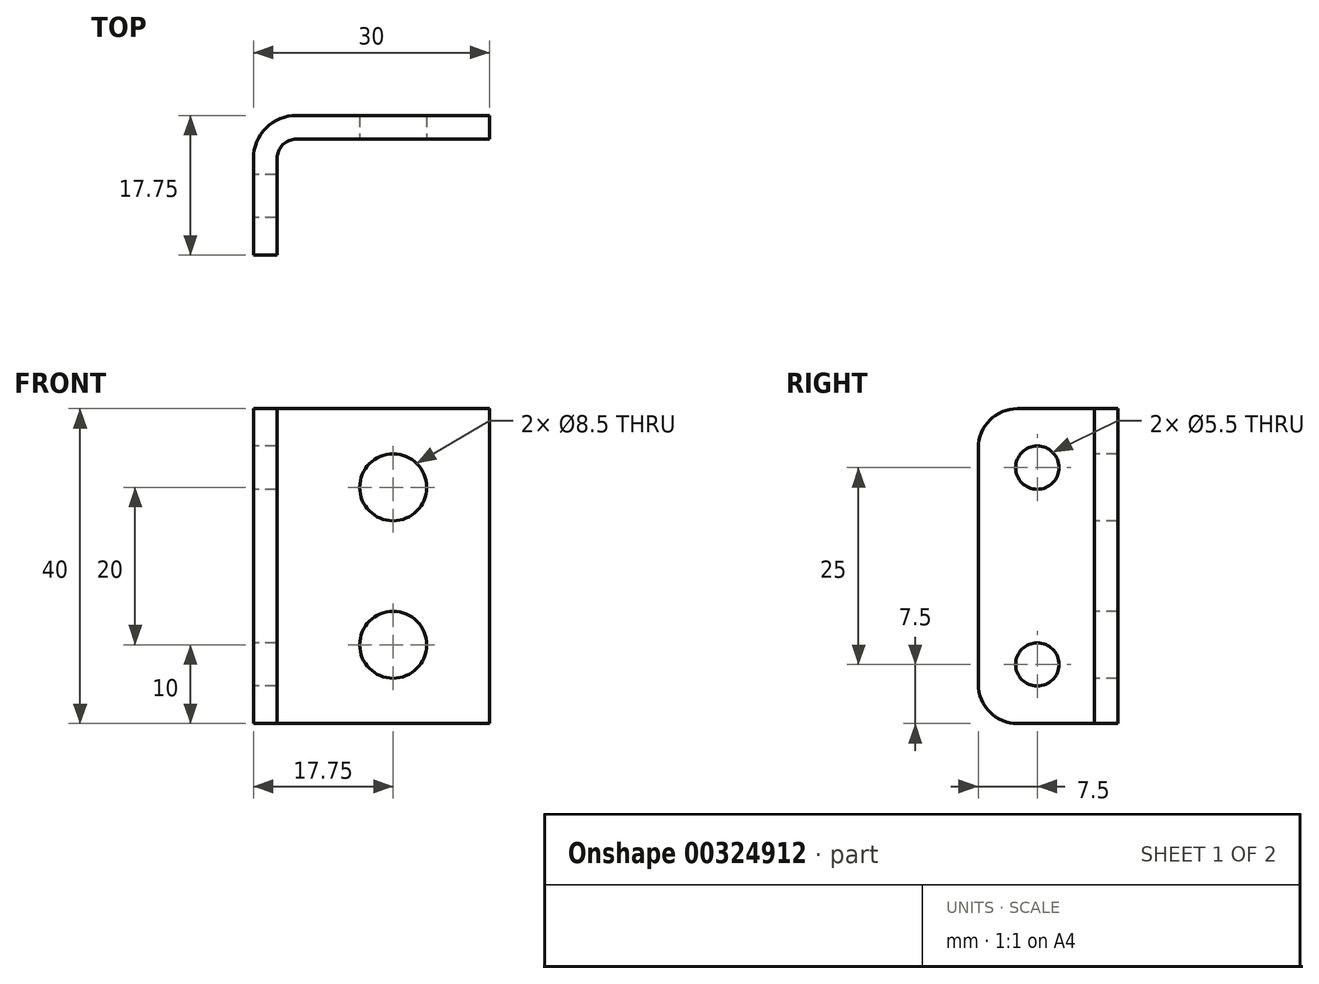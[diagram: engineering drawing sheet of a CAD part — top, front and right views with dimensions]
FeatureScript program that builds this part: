
annotation { "Feature Type Name" : "Feature", "Feature Type Description" : "" }
export const myFeature = defineFeature(function(context is Context, id is Id, definition is map)
    precondition{}
    {
        {
            var Q0;
            Q0=qCreatedBy(makeId("Top.planeOp"),FACE);
            var sketch = newSketch(context, id + "F0", { "sketchPlane" : qUnion([Q0])});
            skLineSegment(sketch, "E0", {"start": v(0, 0) * mm, "end": v(0, 12.25) * mm});
            skLineSegment(sketch, "E1", {"start": v(5.5, 17.75) * mm, "end": v(30, 17.75) * mm});
            skLineSegment(sketch, "E2", {"start": v(30, 17.75) * mm, "end": v(30, 14.75) * mm});
            skLineSegment(sketch, "E3", {"start": v(30, 14.75) * mm, "end": v(5.5, 14.75) * mm});
            skLineSegment(sketch, "E4", {"start": v(3, 12.25) * mm, "end": v(3, 0) * mm});
            skLineSegment(sketch, "E5", {"start": v(3, 0) * mm, "end": v(0, 0) * mm});
            skPoint(sketch, "E6.visualSharp", {"position": v(3, 14.75) * mm});
            skArc(sketch, "E6.filletArc", {"start": v(5.5, 14.75) * mm, "mid": v(3.73, 14.02) * mm, "end": v(3, 12.25) * mm});
            skPoint(sketch, "E7.visualSharp", {"position": v(0, 17.75) * mm});
            skArc(sketch, "E7.filletArc", {"start": v(5.5, 17.75) * mm, "mid": v(1.61, 16.14) * mm, "end": v(0, 12.25) * mm});
            skSolve(sketch);
        }
        {
            var Q0;
            Q0=makeQuery(id+"F0.imprint","IMPRINT",FACE,{"disambiguationData":[TD([[makeQuery(id+"F0.imprint","IMPRINT",EDGE,{"derivedFrom":sQuery(id+"F0.wireOp",EDGE,"E0")}),-1.0]])]});
            extrude(context, id + "F1", {"entities" : qUnion([Q0]), "depth" : 40 * mm});
        }
        {
            var Q0;
            Q0=makeQuery(id+"F1.opExtrude","SWEPT_FACE",FACE,{"disambiguationData":[OSD([sQuery(id+"F0.wireOp",EDGE,"E0")])]});
            var sketch = newSketch(context, id + "F2", { "sketchPlane" : qUnion([Q0])});
            skCircle(sketch, "E8", {"center": v(-7.5, 32.5) * mm, "radius": 2.75 * mm});
            skPoint(sketch, "E8.centerSnap0", {"position": v(-6.12, 40) * mm});
            skCircle(sketch, "E9", {"center": v(-7.5, 7.5) * mm, "radius": 2.75 * mm});
            skSolve(sketch);
        }
        {
            var Q0;
            Q0=makeQuery(id+"F1.opExtrude","SWEPT_FACE",FACE,{"disambiguationData":[OSD([sQuery(id+"F0.wireOp",EDGE,"E3")])]});
            var sketch = newSketch(context, id + "F3", { "sketchPlane" : qUnion([Q0])});
            skCircle(sketch, "E10", {"center": v(17.75, 30) * mm, "radius": 4.25 * mm});
            skPoint(sketch, "E10.centerSnap0", {"position": v(17.75, 40) * mm});
            skCircle(sketch, "E11", {"center": v(17.75, 10) * mm, "radius": 4.25 * mm});
            skSolve(sketch);
        }
        {
            var Q0;
            Q0=makeQuery(id+"F2.imprint","IMPRINT",FACE,{"disambiguationData":[TD([[makeQuery(id+"F2.imprint","IMPRINT",EDGE,{"derivedFrom":sQuery(id+"F2.wireOp",EDGE,"E8")}),1.0]])]});
            var Q1;
            Q1=makeQuery(id+"F2.imprint","IMPRINT",FACE,{"disambiguationData":[TD([[makeQuery(id+"F2.imprint","IMPRINT",EDGE,{"derivedFrom":sQuery(id+"F2.wireOp",EDGE,"E9")}),1.0]])]});
            extrude(context, id + "F4", {"entities" : qUnion([Q0, Q1]), "operationType" : NewBodyOperationType.REMOVE, "endBound" : BoundingType.THROUGH_ALL, "oppositeDirection" : true, "depth" : 25 * mm});
        }
        {
            var Q0;
            Q0=makeQuery(id+"F3.imprint","IMPRINT",FACE,{"disambiguationData":[TD([[makeQuery(id+"F3.imprint","IMPRINT",EDGE,{"derivedFrom":sQuery(id+"F3.wireOp",EDGE,"E11")}),1.0]])]});
            var Q1;
            Q1=makeQuery(id+"F3.imprint","IMPRINT",FACE,{"disambiguationData":[TD([[makeQuery(id+"F3.imprint","IMPRINT",EDGE,{"derivedFrom":sQuery(id+"F3.wireOp",EDGE,"E10")}),1.0]])]});
            extrude(context, id + "F5", {"entities" : qUnion([Q0, Q1]), "operationType" : NewBodyOperationType.REMOVE, "endBound" : BoundingType.THROUGH_ALL, "oppositeDirection" : true, "depth" : 25 * mm});
        }
        {
            var Q0;
            Q0=makeQuery(id+"F1.opExtrude","CAP_EDGE",EDGE,{"disambiguationData":[OSD([sQuery(id+"F0.wireOp",EDGE,"E5")])],"isStart":false});
            var Q1;
            Q1=makeQuery(id+"F1.opExtrude","CAP_EDGE",EDGE,{"disambiguationData":[OSD([sQuery(id+"F0.wireOp",EDGE,"E5")])],"isStart":true});
            fillet(context, id + "F6", {"entities" : qUnion([Q0, Q1]), "radius" : 5 * mm, "tangentPropagation" : true, "allowEdgeOverflow" : false});
        }
    });
